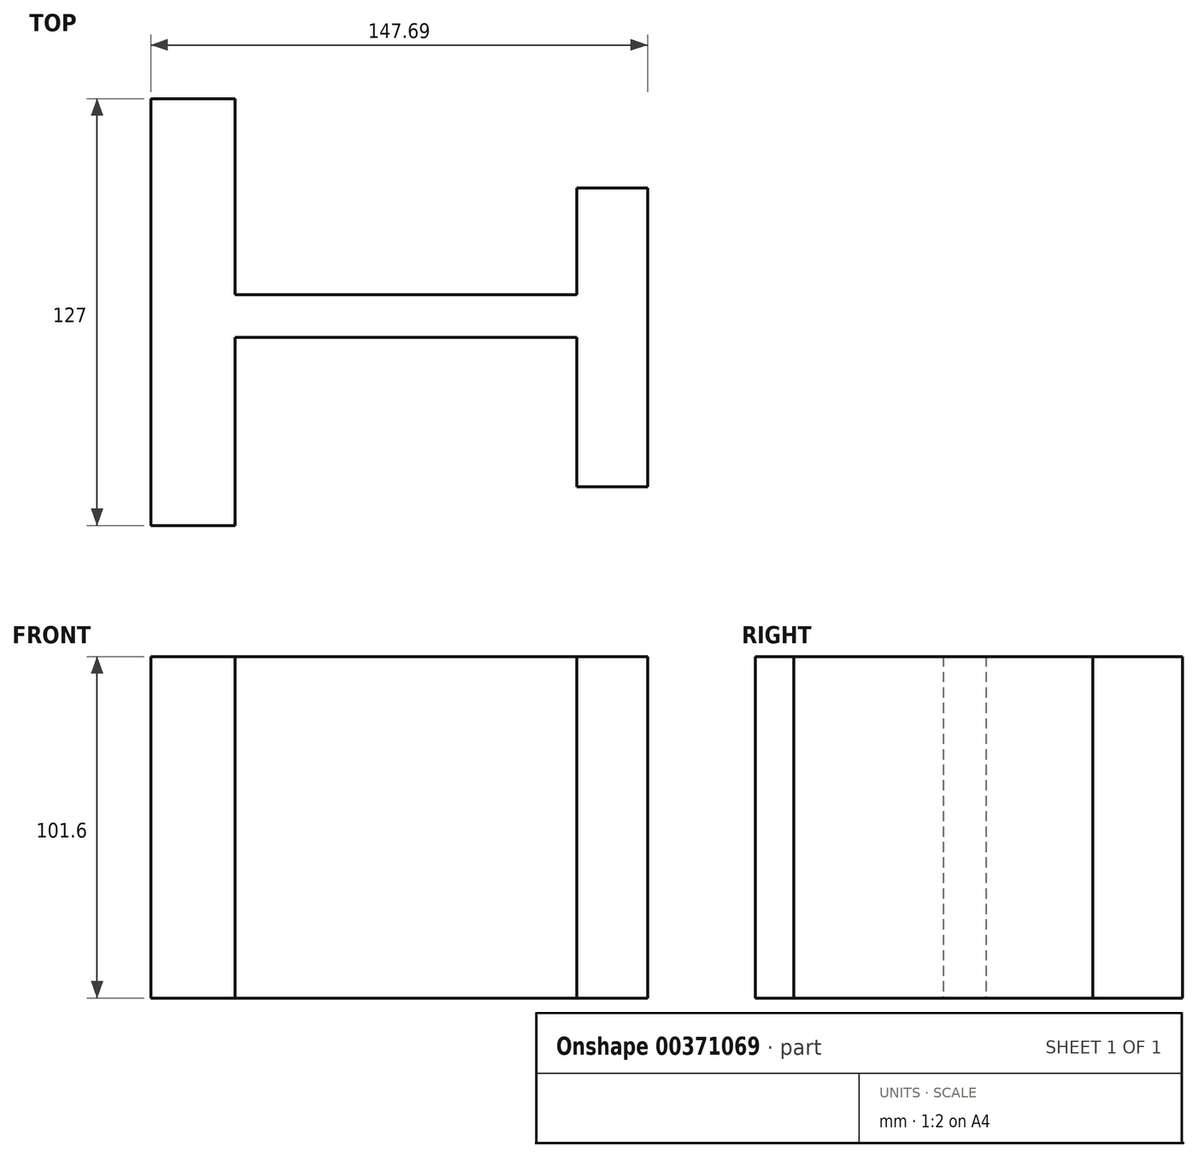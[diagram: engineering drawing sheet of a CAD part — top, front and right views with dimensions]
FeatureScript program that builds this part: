
annotation { "Feature Type Name" : "Feature", "Feature Type Description" : "" }
export const myFeature = defineFeature(function(context is Context, id is Id, definition is map)
    precondition{}
    {
        {
            var Q0;
            Q0=qCreatedBy(makeId("Top.planeOp"),FACE);
            var sketch = newSketch(context, id + "F0", { "sketchPlane" : qUnion([Q0])});
            skLineSegment(sketch, "E0.bottom", {"start": v(-58.47, 62.58) * mm, "end": v(-33.38, 62.58) * mm});
            skLineSegment(sketch, "E0.top", {"start": v(-58.47, -64.42) * mm, "end": v(-33.38, -64.42) * mm});
            skLineSegment(sketch, "E0.left", {"start": v(-58.47, 62.58) * mm, "end": v(-58.47, -64.42) * mm});
            skLineSegment(sketch, "E0.right", {"start": v(-33.38, 62.58) * mm, "end": v(-33.38, -64.42) * mm});
            skLineSegment(sketch, "E1.bottom", {"start": v(68.22, 35.94) * mm, "end": v(89.22, 35.94) * mm});
            skLineSegment(sketch, "E1.top", {"start": v(68.22, -52.96) * mm, "end": v(89.22, -52.96) * mm});
            skLineSegment(sketch, "E1.left", {"start": v(68.22, 35.94) * mm, "end": v(68.22, -52.96) * mm});
            skLineSegment(sketch, "E1.right", {"start": v(89.22, 35.94) * mm, "end": v(89.22, -52.96) * mm});
            skLineSegment(sketch, "E2.bottom", {"start": v(-33.38, 4.2) * mm, "end": v(68.22, 4.2) * mm});
            skLineSegment(sketch, "E2.top", {"start": v(-33.38, -8.5) * mm, "end": v(68.22, -8.5) * mm});
            skLineSegment(sketch, "E2.left", {"start": v(-33.38, 4.2) * mm, "end": v(-33.38, -8.5) * mm});
            skLineSegment(sketch, "E2.right", {"start": v(68.22, 4.2) * mm, "end": v(68.22, -8.5) * mm});
            skSolve(sketch);
        }
        {
            var Q0;
            {var subQ3=sQuery(id+"F0.wireOp",EDGE,"E1.bottom");Q0=makeQuery(id+"F0.imprint","IMPRINT",FACE,{"disambiguationData":[TD([[makeQuery(id+"F0.imprint","IMPRINT",EDGE,{"derivedFrom":subQ3}),-1.0]])]});}
            var Q1;
            {var subQ1=sQuery(id+"F0.wireOp",EDGE,"E0.bottom");Q1=makeQuery(id+"F0.imprint","IMPRINT",FACE,{"disambiguationData":[TD([[makeQuery(id+"F0.imprint","IMPRINT",EDGE,{"derivedFrom":subQ1}),-1.0]])]});}
            var Q2;
            Q2=makeQuery(id+"F0.imprint","IMPRINT",FACE,{"disambiguationData":[TD([[makeQuery(id+"F0.imprint","IMPRINT",EDGE,{"derivedFrom":sQuery(id+"F0.wireOp",EDGE,"E2.bottom")}),-1.0]])]});
            extrude(context, id + "F1", {"entities" : qUnion([Q0, Q1, Q2]), "depth" : 101.6 * mm});
        }
    });
